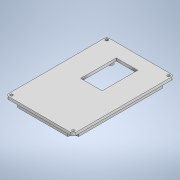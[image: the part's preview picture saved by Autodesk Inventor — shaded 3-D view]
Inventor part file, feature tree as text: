
AUTODESK INVENTOR PART (.ipt)
format: ipt  version: 2020.2 (Build 242310000, 310)  size: 200,704 bytes
history: native  units: mm
features: sketch x4, extrude x4, fillet x1
ambient origin geometry x8: Origin, YZ Plane, XZ Plane, XY Plane, X Axis, Y Axis, Z Axis, Center Point
bodies: Solid1 (feature_tree)
feature tree (9):
  sketch  "Sketch1"  dims[d0=75.0mm d1=50.0mm]
  extrude  "Extrusion1"  Depth=50.0mm
  extrude  "Extrusion4"  Depth=2.0mm
  extrude  "Extrusion5"  Depth=2.0mm
  extrude  "Extrusion6"  Depth=2.0mm
  fillet  "Fillet2"  Radius=2.0mm
  sketch  "Sketch4"  dims[d4=2.0mm d5=0.0mm d17=2.0mm]
  sketch  "Sketch5"  dims[d18=2.0mm d21=2.0mm]
  sketch  "Sketch6"  dims[d22=2.0mm d23=2.0mm d25=2.0mm d26=2.0mm d27=2.0mm d28=2.0mm d29=2.2mm d30=2.2mm d32=4.0mm d33=4.0mm d34=0.0mm d35=2.0mm d36=23.25mm d37=23.0mm d38=2.0mm d39=4.0mm d40=2.0mm d41=0.0mm d42=16.0mm d43=26.5mm d45=1.5mm d46=10.0mm d47=0.0mm d48=2.0mm]
